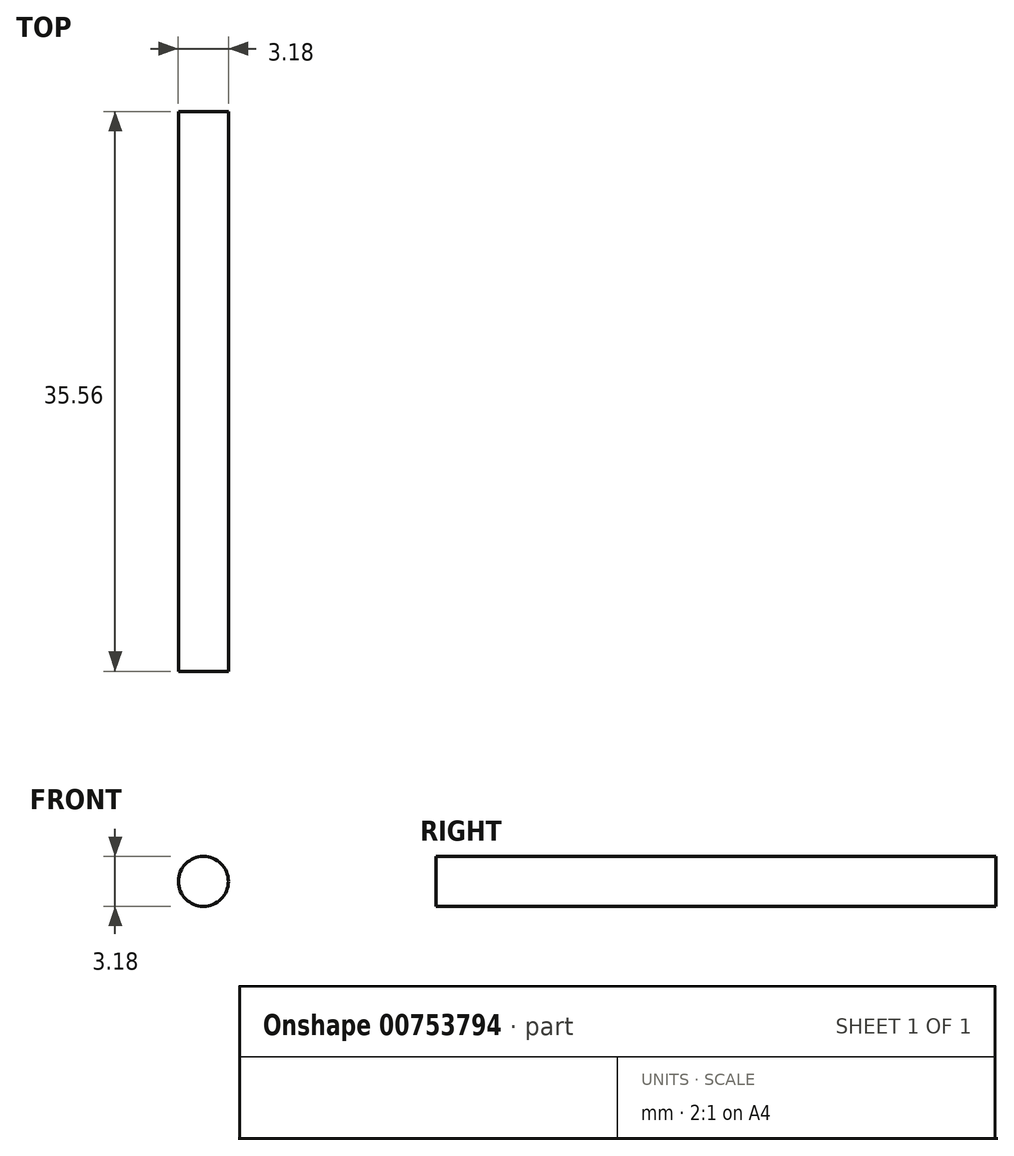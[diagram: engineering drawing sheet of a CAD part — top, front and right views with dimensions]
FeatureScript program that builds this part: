
annotation { "Feature Type Name" : "Feature", "Feature Type Description" : "" }
export const myFeature = defineFeature(function(context is Context, id is Id, definition is map)
    precondition{}
    {
        {
            var Q0;
            Q0=qCreatedBy(makeId("Front.planeOp"),FACE);
            var sketch = newSketch(context, id + "F0", { "sketchPlane" : qUnion([Q0])});
            skCircle(sketch, "E0", {"center": v(-62.72, 47.2) * mm, "radius": 1.59 * mm});
            skSolve(sketch);
        }
        {
            var Q0;
            Q0=makeQuery(id+"F0.imprint","IMPRINT",FACE,{"disambiguationData":[TD([[makeQuery(id+"F0.imprint","IMPRINT",EDGE,{"derivedFrom":sQuery(id+"F0.wireOp",EDGE,"E0")}),1.0]])]});
            extrude(context, id + "F1", {"entities" : qUnion([Q0]), "depth" : 35.56 * mm, "offsetDistance" : 25.4 * mm});
        }
    });
